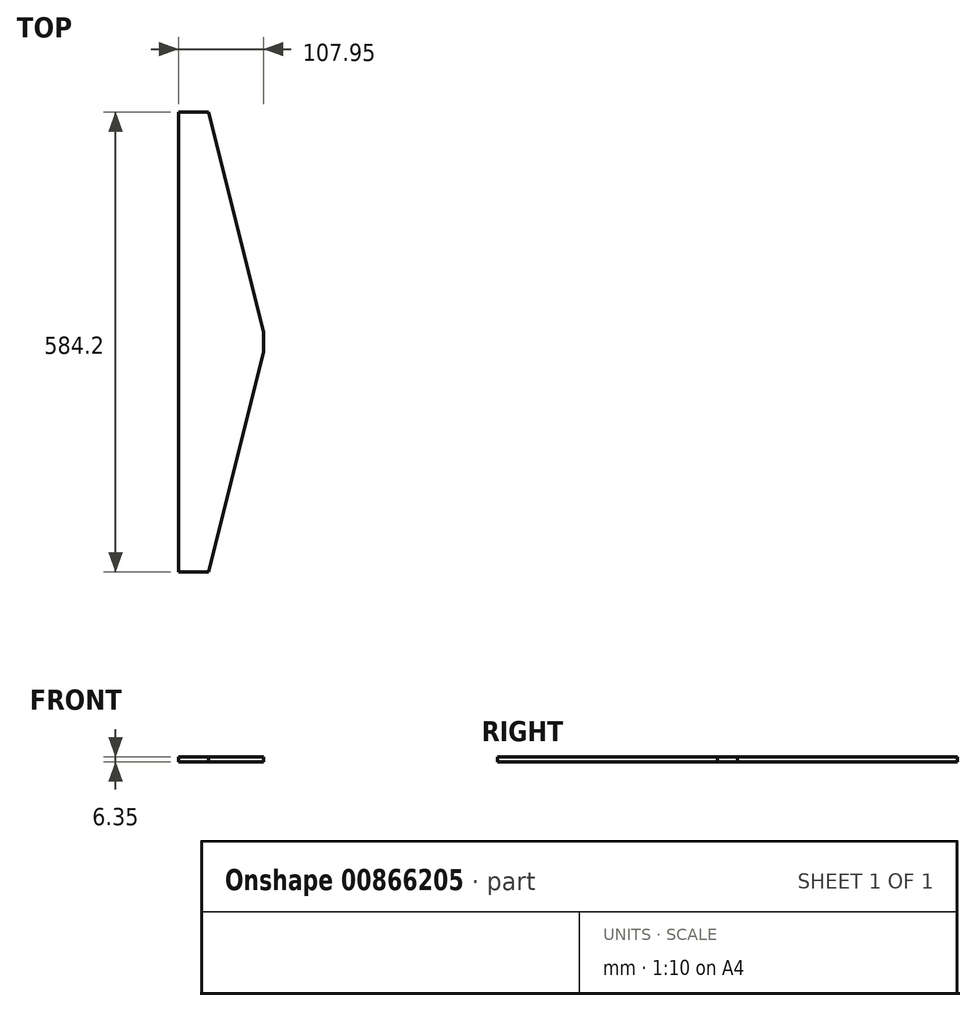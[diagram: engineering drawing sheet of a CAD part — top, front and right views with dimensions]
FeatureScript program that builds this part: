
annotation { "Feature Type Name" : "Feature", "Feature Type Description" : "" }
export const myFeature = defineFeature(function(context is Context, id is Id, definition is map)
    precondition{}
    {
        {
            var Q0;
            Q0=qCreatedBy(makeId("Top.planeOp"),FACE);
            var sketch = newSketch(context, id + "F0", { "sketchPlane" : qUnion([Q0])});
            skLineSegment(sketch, "E0", {"start": v(0, 0) * mm, "end": v(-107.95, 0) * mm});
            skLineSegment(sketch, "E1", {"start": v(-107.95, 0) * mm, "end": v(-107.95, -279.4) * mm});
            skLineSegment(sketch, "E2", {"start": v(-107.95, -279.4) * mm, "end": v(-69.85, -279.4) * mm});
            skLineSegment(sketch, "E3", {"start": v(0, 0) * mm, "end": v(-69.85, -279.4) * mm});
            skPoint(sketch, "E4.MirrorCS.end.orphan", {"position": v(-69.85, 279.4) * mm});
            skPoint(sketch, "E4.MirrorCS.start.orphan", {"position": v(0, 0) * mm});
            skPoint(sketch, "E5.MirrorCS.end.orphan", {"position": v(-107.95, 279.4) * mm});
            skPoint(sketch, "E5.MirrorCS.start.orphan", {"position": v(-107.95, 0) * mm});
            skLineSegment(sketch, "E6", {"start": v(0, 0) * mm, "end": v(0, 12.7) * mm});
            skLineSegment(sketch, "E7", {"start": v(-107.95, 12.7) * mm, "end": v(-107.95, 0) * mm});
            skLineSegment(sketch, "E8", {"start": v(0, 12.7) * mm, "end": v(-107.95, 12.7) * mm});
            skPoint(sketch, "E9.end.orphan", {"position": v(-107.95, 25.4) * mm});
            skPoint(sketch, "E10.orphan", {"position": v(0, 25.4) * mm});
            skLineSegment(sketch, "E11.MirrorCS", {"start": v(-107.95, 25.4) * mm, "end": v(-107.95, 304.8) * mm});
            skLineSegment(sketch, "E12.MirrorCS", {"start": v(-107.95, 304.8) * mm, "end": v(-69.85, 304.8) * mm});
            skLineSegment(sketch, "E13.MirrorCS", {"start": v(0, 25.4) * mm, "end": v(-69.85, 304.8) * mm});
            skLineSegment(sketch, "E14.MirrorCS", {"start": v(0, 25.4) * mm, "end": v(-107.95, 25.4) * mm});
            skLineSegment(sketch, "E15.MirrorCS", {"start": v(-107.95, 12.7) * mm, "end": v(-107.95, 25.4) * mm});
            skLineSegment(sketch, "E16.MirrorCS", {"start": v(0, 25.4) * mm, "end": v(0, 12.7) * mm});
            skSolve(sketch);
        }
        {
            var Q0;
            Q0=makeQuery(id+"F0.imprint","IMPRINT",FACE,{"disambiguationData":[TD([[makeQuery(id+"F0.imprint","IMPRINT",EDGE,{"derivedFrom":sQuery(id+"F0.wireOp",EDGE,"E0")}),1.0]])]});
            var Q1;
            Q1=makeQuery(id+"F0.imprint","IMPRINT",FACE,{"disambiguationData":[TD([[makeQuery(id+"F0.imprint","IMPRINT",EDGE,{"derivedFrom":sQuery(id+"F0.wireOp",EDGE,"E11.MirrorCS")}),-1.0]])]});
            var Q2;
            Q2=makeQuery(id+"F0.imprint","IMPRINT",FACE,{"disambiguationData":[TD([[makeQuery(id+"F0.imprint","IMPRINT",EDGE,{"derivedFrom":sQuery(id+"F0.wireOp",EDGE,"E8")}),-1.0]])]});
            var Q3;
            Q3=makeQuery(id+"F0.imprint","IMPRINT",FACE,{"disambiguationData":[TD([[makeQuery(id+"F0.imprint","IMPRINT",EDGE,{"derivedFrom":sQuery(id+"F0.wireOp",EDGE,"E0")}),-1.0]])]});
            extrude(context, id + "F1", {"entities" : qUnion([Q0, Q1, Q2, Q3]), "depth" : 6.35 * mm, "offsetDistance" : 25.4 * mm});
        }
    });
